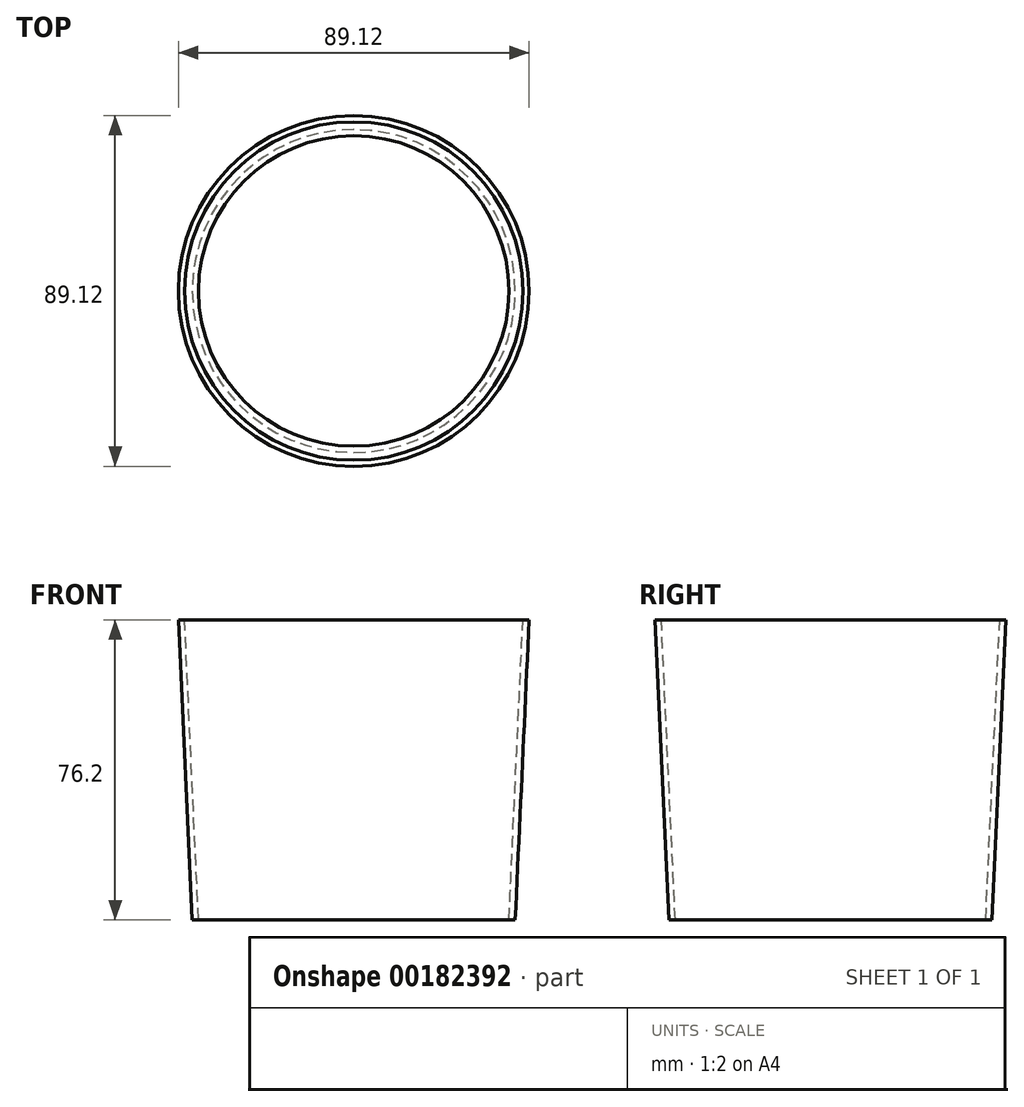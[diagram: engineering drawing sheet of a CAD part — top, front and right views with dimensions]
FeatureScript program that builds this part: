
annotation { "Feature Type Name" : "Feature", "Feature Type Description" : "" }
export const myFeature = defineFeature(function(context is Context, id is Id, definition is map)
    precondition{}
    {
        {
            var Q0;
            Q0=qCreatedBy(makeId("Top.planeOp"),FACE);
            var sketch = newSketch(context, id + "F0", { "sketchPlane" : qUnion([Q0])});
            skCircle(sketch, "E0", {"center": v(0, 0) * mm, "radius": 39.43 * mm});
            skSolve(sketch);
        }
        {
            var Q0;
            Q0=qCreatedBy(makeId("Top.planeOp"),FACE);
            cPlane(context, id + "F1", {"entities" : qUnion([Q0]), "cplaneType" : CPlaneType.OFFSET, "offset" : 76.2 * mm, "width" : 152.4 * mm, "height" : 152.4 * mm});
        }
        {
            var Q0;
            Q0=qCreatedBy(id+"F1.planeOp",FACE);
            var sketch = newSketch(context, id + "F2", { "sketchPlane" : qUnion([Q0])});
            skCircle(sketch, "E1", {"center": v(0, 0) * mm, "radius": 42.98 * mm});
            skSolve(sketch);
        }
        {
            var Q0;
            Q0=qCreatedBy(makeId("Top.planeOp"),FACE);
            var sketch = newSketch(context, id + "F3", { "sketchPlane" : qUnion([Q0])});
            skCircle(sketch, "E2", {"center": v(0, 0) * mm, "radius": 41.02 * mm});
            skSolve(sketch);
        }
        {
            var Q0;
            Q0=qCreatedBy(id+"F1.planeOp",FACE);
            var sketch = newSketch(context, id + "F4", { "sketchPlane" : qUnion([Q0])});
            skCircle(sketch, "E3", {"center": v(0, 0) * mm, "radius": 44.56 * mm});
            skSolve(sketch);
        }
        {
            var Q0;
            Q0=makeQuery(id+"F4.imprint","IMPRINT",FACE,{"disambiguationData":[TD([[makeQuery(id+"F4.imprint","IMPRINT",EDGE,{"derivedFrom":sQuery(id+"F4.wireOp",EDGE,"E3")}),1.0]])]});
            var Q1;
            Q1=makeQuery(id+"F3.imprint","IMPRINT",FACE,{"disambiguationData":[TD([[makeQuery(id+"F3.imprint","IMPRINT",EDGE,{"derivedFrom":sQuery(id+"F3.wireOp",EDGE,"E2")}),1.0]])]});
            loft(context, id + "F5", {"sheetProfilesArray" : [{ "sheetProfileEntities" : qUnion([Q0]) }, { "sheetProfileEntities" : qUnion([Q1]) }]});
        }
        {
            var Q1;
            Q1=makeQuery(id+"F0.imprint","IMPRINT",FACE,{"disambiguationData":[TD([[makeQuery(id+"F0.imprint","IMPRINT",EDGE,{"derivedFrom":sQuery(id+"F0.wireOp",EDGE,"E0")}),1.0]])]});
            var Q2;
            Q2=makeQuery(id+"F2.imprint","IMPRINT",FACE,{"disambiguationData":[TD([[makeQuery(id+"F2.imprint","IMPRINT",EDGE,{"derivedFrom":sQuery(id+"F2.wireOp",EDGE,"E1")}),1.0]])]});
            loft(context, id + "F6", {"operationType" : NewBodyOperationType.REMOVE, "sheetProfilesArray" : [{ "sheetProfileEntities" : qUnion([Q1]) }, { "sheetProfileEntities" : qUnion([Q2]) }]});
        }
    });
